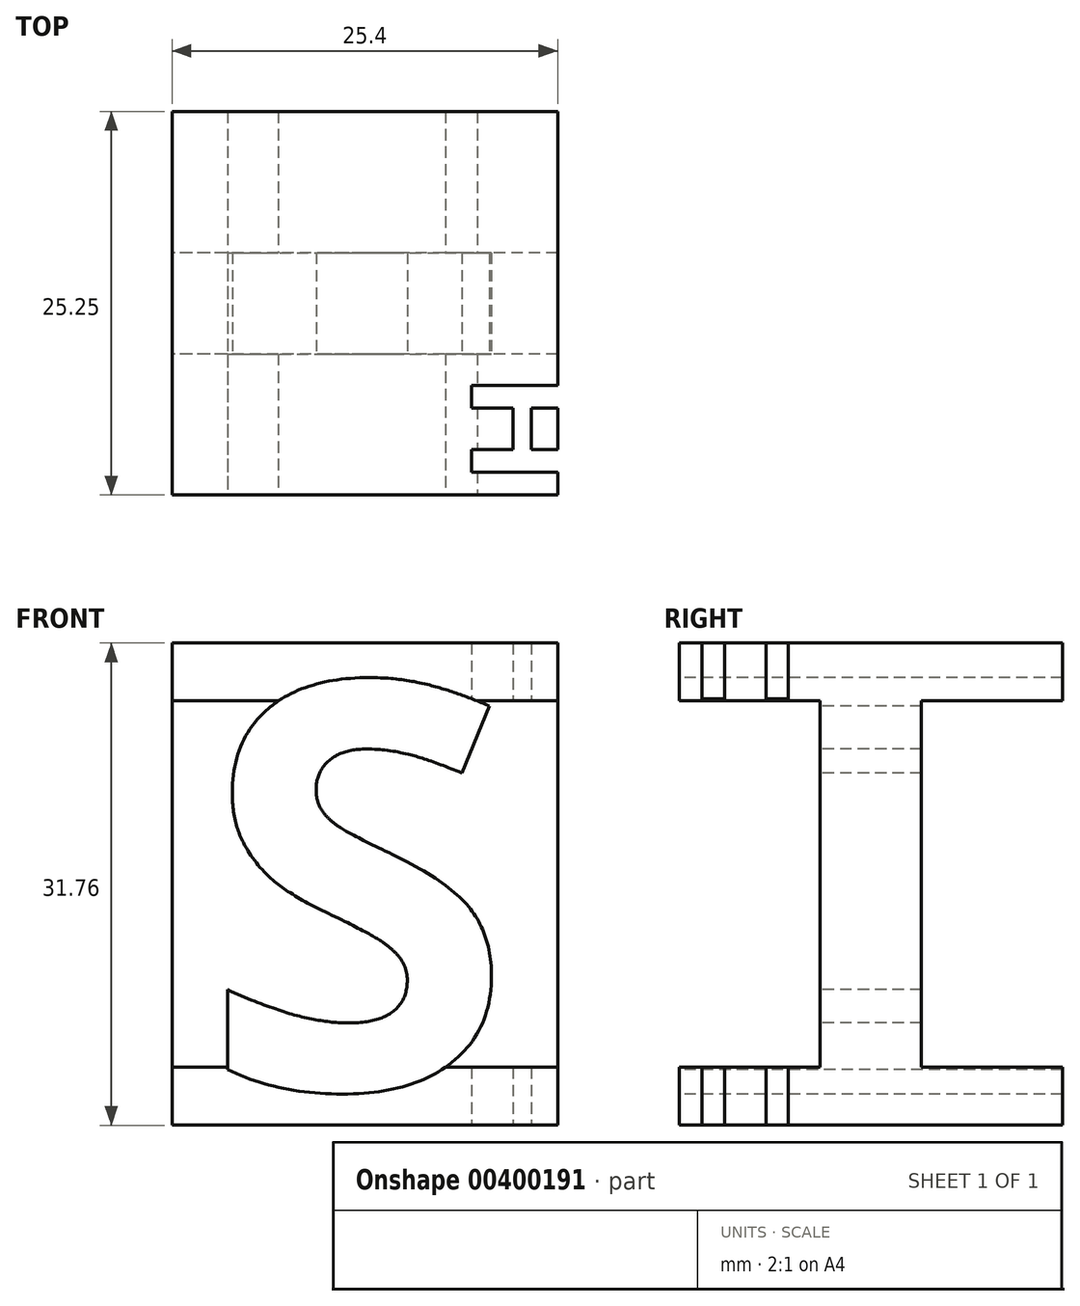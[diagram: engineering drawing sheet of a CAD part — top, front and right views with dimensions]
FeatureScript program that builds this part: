
annotation { "Feature Type Name" : "Feature", "Feature Type Description" : "" }
export const myFeature = defineFeature(function(context is Context, id is Id, definition is map)
    precondition{}
    {
        {
            var Q0;
            Q0=qCreatedBy(makeId("Front.planeOp"),FACE);
            var sketch = newSketch(context, id + "F0", { "sketchPlane" : qUnion([Q0])});
            skLineSegment(sketch, "E0.bottom", {"start": v(12.7, 15.88) * mm, "end": v(-12.7, 15.88) * mm});
            skLineSegment(sketch, "E0.top", {"start": v(12.7, -15.88) * mm, "end": v(-12.7, -15.88) * mm});
            skLineSegment(sketch, "E0.left", {"start": v(12.7, 15.88) * mm, "end": v(12.7, -15.88) * mm});
            skLineSegment(sketch, "E0.right", {"start": v(-12.7, 15.88) * mm, "end": v(-12.7, -15.88) * mm});
            skPoint(sketch, "E0.middle", {"position": v(0, 0) * mm});
            skSolve(sketch);
        }
        {
            var Q0;
            Q0=qSketchRegion(id+"F0",true);
            extrude(context, id + "F1", {"entities" : qUnion([Q0]), "depth" : 31.75 * mm});
        }
        {
            var Q0;
            Q0=makeQuery(id+"F1.opExtrude","SWEPT_FACE",FACE,{"disambiguationData":[OSD([sQuery(id+"F0.wireOp",EDGE,"E0.right")])]});
            var sketch = newSketch(context, id + "F2", { "sketchPlane" : qUnion([Q0])});
            skText(sketch, "E1", { "text": "I", "fontName": "OpenSans-Bold.ttf"});
            skLineSegment(sketch, "E2.bottom", {"start": v(3.25, -15.88) * mm, "end": v(28.5, -15.88) * mm});
            skLineSegment(sketch, "E2.top", {"start": v(3.25, -12.07) * mm, "end": v(28.5, -12.07) * mm});
            skLineSegment(sketch, "E2.left", {"start": v(3.25, -15.88) * mm, "end": v(3.25, -12.07) * mm});
            skLineSegment(sketch, "E2.right", {"start": v(28.5, -15.87) * mm, "end": v(28.5, -12.07) * mm});
            skPoint(sketch, "E3", {"position": v(0, 0) * mm});
            skPoint(sketch, "E4", {"position": v(31.75, 0) * mm});
            skPoint(sketch, "E5", {"position": v(15.88, 15.88) * mm});
            skPoint(sketch, "E6", {"position": v(15.88, -15.88) * mm});
            skLineSegment(sketch, "E7", {"start": v(15.88, 15.88) * mm, "end": v(15.88, -15.88) * mm, "construction": true});
            skPoint(sketch, "E8", {"position": v(15.88, -12.07) * mm});
            skLineSegment(sketch, "E9.bottom", {"start": v(3.25, 15.88) * mm, "end": v(28.5, 15.88) * mm});
            skLineSegment(sketch, "E9.top", {"start": v(3.25, 12.06) * mm, "end": v(28.5, 12.06) * mm});
            skLineSegment(sketch, "E9.left", {"start": v(3.25, 15.87) * mm, "end": v(3.25, 12.06) * mm});
            skLineSegment(sketch, "E9.right", {"start": v(28.5, 15.88) * mm, "end": v(28.5, 12.06) * mm});
            skPoint(sketch, "E10", {"position": v(15.88, 12.06) * mm});
            const initialGuessF2  = {"E1": [0.00858, -0.01588, 1, 0, 0.03175]};
            skSetInitialGuess(sketch, initialGuessF2);
            skSolve(sketch);
        }
        {
            var Q0;
            {var subQ4=sQuery(id+"F2.wireOp",EDGE,"E2.right");Q0=makeQuery(id+"F2.imprint","IMPRINT",FACE,{"disambiguationData":[TD([[makeQuery(id+"F2.imprint","IMPRINT",EDGE,{"derivedFrom":subQ4}),-1.0]])]});}
            var Q1;
            {var subQ0=sQuery(id+"F2.wireOp",EDGE,"E2.left");Q1=makeQuery(id+"F2.imprint","IMPRINT",FACE,{"disambiguationData":[TD([[makeQuery(id+"F2.imprint","IMPRINT",EDGE,{"derivedFrom":subQ0}),1.0]])]});}
            extrude(context, id + "F3", {"entities" : qUnion([Q0, Q1]), "operationType" : NewBodyOperationType.REMOVE, "endBound" : BoundingType.THROUGH_ALL, "oppositeDirection" : true, "depth" : 25.4 * mm});
        }
        {
            var Q0;
            Q0=makeQuery(id+"F3.boolean.opBoolean","COPY",FACE,{"derivedFrom":makeQuery(id+"F3.opExtrude","SWEPT_FACE",FACE,{"disambiguationData":[OSD([sQuery(id+"F2.wireOp",EDGE,"E1.sketch_text.stroke-2")])]})});
            var sketch = newSketch(context, id + "F4", { "sketchPlane" : qUnion([Q0])});
            skText(sketch, "E11", { "text": "S", "fontName": "OpenSans-Bold.ttf"});
            skLineSegment(sketch, "E12.bottom", {"start": v(-10.2, -15.88) * mm, "end": v(9.34, -15.88) * mm, "construction": true});
            skLineSegment(sketch, "E12.top", {"start": v(-10.2, -15.37) * mm, "end": v(9.34, -15.37) * mm, "construction": true});
            skLineSegment(sketch, "E12.left", {"start": v(-10.2, -15.88) * mm, "end": v(-10.2, -15.37) * mm, "construction": true});
            skLineSegment(sketch, "E12.right", {"start": v(9.34, -15.88) * mm, "end": v(9.34, -15.37) * mm, "construction": true});
            const initialGuessF4  = {"E11": [-0.01076, -0.01345, 1, 0, 0.0269]};
            skSetInitialGuess(sketch, initialGuessF4);
            skSolve(sketch);
        }
        {
            var Q0;
            Q0 = qSketchRegion(id + "F4", true);
            extrude(context, id + "F5", {"entities" : qUnion([Q0]), "operationType" : NewBodyOperationType.REMOVE, "endBound" : BoundingType.THROUGH_ALL, "oppositeDirection" : true, "depth" : 25.4 * mm, "hasSecondDirection" : true, "secondDirectionBound" : SecondDirectionBoundingType.THROUGH_ALL, "secondDirectionOppositeDirection" : false, "secondDirectionDepth" : 25.4 * mm});
        }
        {
            var Q0;
            {var subQ0=sQuery(id+"F4.wireOp",EDGE,"E12.top");Q0=makeQuery(id+"F5.boolean.opBoolean","MERGE",FACE,{"derivedFrom":[makeQuery(id+"F3.boolean.opBoolean","COPY",FACE,{"derivedFrom":makeQuery(id+"F3.opExtrude","SWEPT_FACE",FACE,{"disambiguationData":[OSD([sQuery(id+"F2.wireOp",EDGE,"E2.top")])]})}),makeQuery(id+"F5.opExtrude","SWEPT_FACE",FACE,{"disambiguationData":[OSD([subQ0]),TDD([makeQuery(id+"F4.imprint","IMPRINT",EDGE,{"disambiguationData":[TD([[makeQuery(id+"F4.imprint","INTERSECT",VERTEX,{"derivedFrom":[subQ0,sQuery(id+"F4.wireOp",EDGE,"E12.left")]}),-1.0]])],"derivedFrom":subQ0})])]}),makeQuery(id+"F5.opExtrude","SWEPT_FACE",FACE,{"disambiguationData":[OSD([subQ0]),TDD([makeQuery(id+"F4.imprint","IMPRINT",EDGE,{"disambiguationData":[TD([[makeQuery(id+"F4.imprint","INTERSECT",VERTEX,{"derivedFrom":[subQ0,sQuery(id+"F4.wireOp",EDGE,"E12.right")]}),1.0]])],"derivedFrom":subQ0})])]})]});}
            var sketch = newSketch(context, id + "F6", { "sketchPlane" : qUnion([Q0])});
            skText(sketch, "E13", { "text": "H", "fontName": "OpenSans-Bold.ttf"});
            const initialGuessF6  = {"E13": [0.01397, -0.02786, 0, 1, 0.007]};
            skSetInitialGuess(sketch, initialGuessF6);
            skSolve(sketch);
        }
        {
            var Q0;
            Q0 = qSketchRegion(id + "F6", true);
            extrude(context, id + "F7", {"entities" : qUnion([Q0]), "operationType" : NewBodyOperationType.REMOVE, "endBound" : BoundingType.THROUGH_ALL, "depth" : 25.4 * mm, "hasSecondDirection" : true, "secondDirectionBound" : SecondDirectionBoundingType.THROUGH_ALL, "secondDirectionOppositeDirection" : true, "secondDirectionDepth" : 25.4 * mm});
        }
    });
